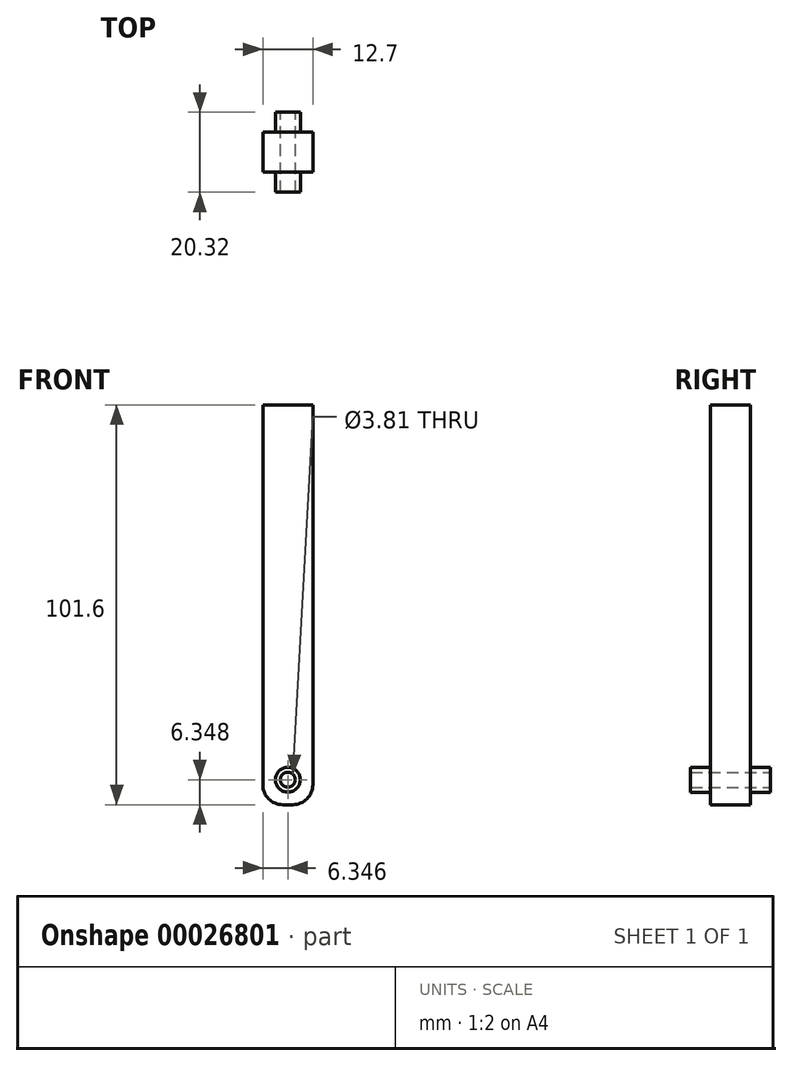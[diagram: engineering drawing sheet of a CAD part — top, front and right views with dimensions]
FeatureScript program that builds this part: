
annotation { "Feature Type Name" : "Feature", "Feature Type Description" : "" }
export const myFeature = defineFeature(function(context is Context, id is Id, definition is map)
    precondition{}
    {
        {
            var Q0;
            Q0=qCreatedBy(makeId("Front.planeOp"),FACE);
            var sketch = newSketch(context, id + "F0", { "sketchPlane" : qUnion([Q0])});
            skLineSegment(sketch, "E0.bottom", {"start": v(-34.74, 62.16) * mm, "end": v(-22.04, 62.16) * mm});
            skLineSegment(sketch, "E0.top", {"start": v(-34.74, -39.44) * mm, "end": v(-22.04, -39.44) * mm});
            skLineSegment(sketch, "E0.left", {"start": v(-34.74, 62.16) * mm, "end": v(-34.74, -39.44) * mm});
            skLineSegment(sketch, "E0.right", {"start": v(-22.04, 62.16) * mm, "end": v(-22.04, -39.44) * mm});
            skLineSegment(sketch, "E1", {"start": v(-28.4, -39.44) * mm, "end": v(-28.4, -33.1) * mm});
            skCircle(sketch, "E2", {"center": v(-28.4, -33.1) * mm, "radius": 1.9 * mm});
            skCircle(sketch, "E3", {"center": v(-28.4, -33.1) * mm, "radius": 3.18 * mm});
            skSolve(sketch);
        }
        {
            var Q0;
            Q0=makeQuery(id+"F0.imprint","IMPRINT",FACE,{"disambiguationData":[TD([[makeQuery(id+"F0.imprint","IMPRINT",EDGE,{"derivedFrom":sQuery(id+"F0.wireOp",EDGE,"E0.bottom")}),-1.0]])]});
            extrude(context, id + "F1", {"entities" : qUnion([Q0]), "depth" : 10.16 * mm});
        }
        {
            var Q0;
            Q0=makeQuery(id+"F0.imprint","IMPRINT",FACE,{"disambiguationData":[TD([[makeQuery(id+"F0.imprint","IMPRINT",EDGE,{"derivedFrom":sQuery(id+"F0.wireOp",EDGE,"E2")}),-1.0]])]});
            extrude(context, id + "F2", {"entities" : qUnion([Q0]), "operationType" : NewBodyOperationType.ADD, "depth" : 15.24 * mm});
        }
        {
            var Q0;
            Q0=makeQuery(id+"F0.imprint","IMPRINT",FACE,{"disambiguationData":[TD([[makeQuery(id+"F0.imprint","IMPRINT",EDGE,{"derivedFrom":sQuery(id+"F0.wireOp",EDGE,"E2")}),-1.0]])]});
            extrude(context, id + "F3", {"entities" : qUnion([Q0]), "operationType" : NewBodyOperationType.ADD, "oppositeDirection" : true, "depth" : 5.08 * mm});
        }
        {
            var Q0;
            Q0=makeQuery(id+"F1.opExtrude","SWEPT_EDGE",EDGE,{"disambiguationData":[OSD([sQuery(id+"F0.wireOp",EDGE,"E0.top"),sQuery(id+"F0.wireOp",EDGE,"E0.left")])]});
            fillet(context, id + "F4", {"entities" : qUnion([Q0]), "radius" : 5.08 * mm, "tangentPropagation" : true, "allowEdgeOverflow" : false});
        }
        {
            var Q0;
            Q0=makeQuery(id+"F1.opExtrude","SWEPT_EDGE",EDGE,{"disambiguationData":[OSD([sQuery(id+"F0.wireOp",EDGE,"E0.top"),sQuery(id+"F0.wireOp",EDGE,"E0.right")])]});
            fillet(context, id + "F5", {"entities" : qUnion([Q0]), "radius" : 5.08 * mm, "tangentPropagation" : true, "allowEdgeOverflow" : false});
        }
    });
